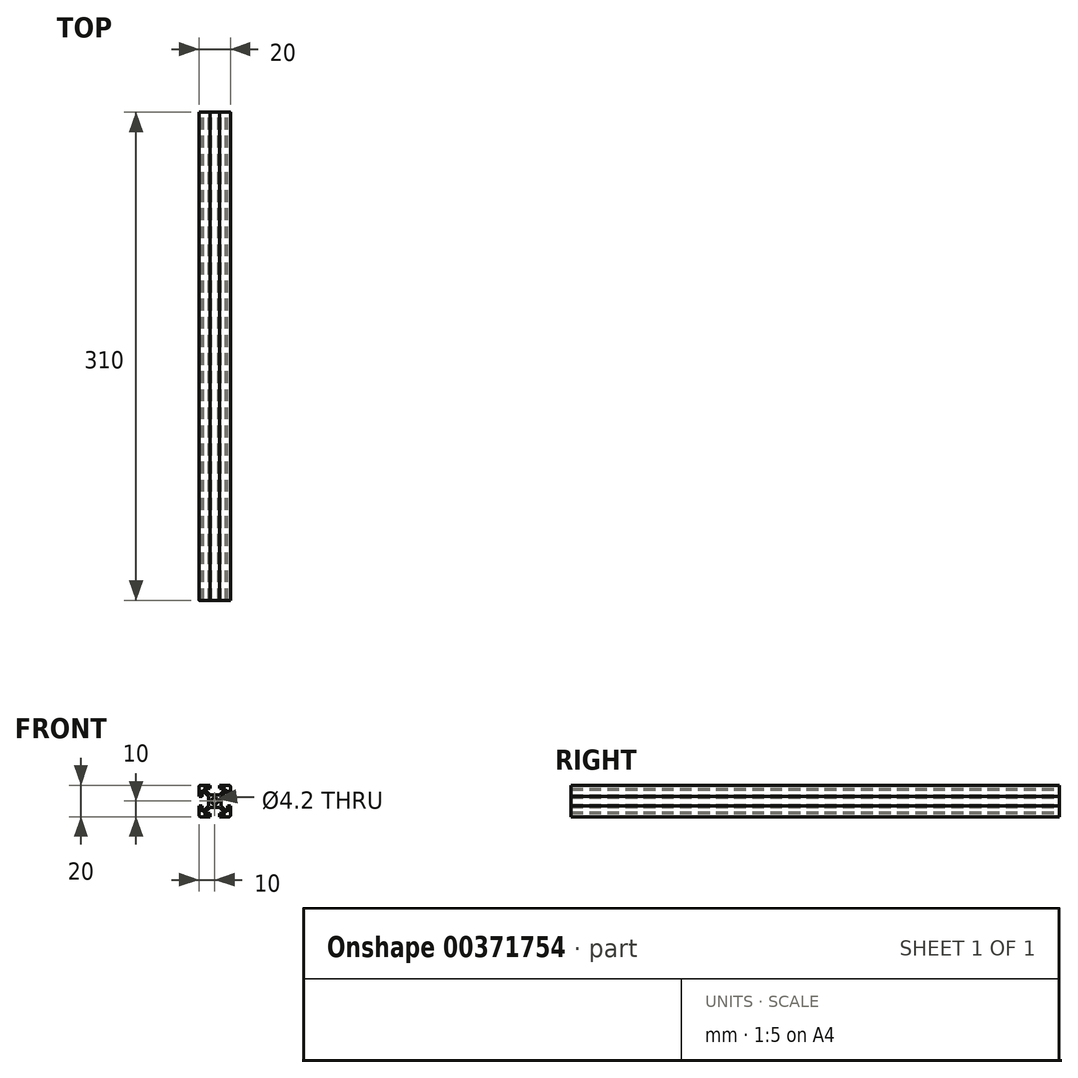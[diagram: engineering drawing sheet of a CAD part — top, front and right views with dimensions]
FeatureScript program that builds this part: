
annotation { "Feature Type Name" : "Feature", "Feature Type Description" : "" }
export const myFeature = defineFeature(function(context is Context, id is Id, definition is map)
    precondition{}
    {
        {
            var Q0;
            Q0=qCreatedBy(makeId("Front.planeOp"),FACE);
            var sketch = newSketch(context, id + "F0", { "sketchPlane" : qUnion([Q0])});
            skLineSegment(sketch, "E0.top", {"start": v(-9, -10) * mm, "end": v(-3, -10) * mm});
            skLineSegment(sketch, "E0.left", {"start": v(-10, 9) * mm, "end": v(-10, 3.08) * mm});
            skLineSegment(sketch, "E0.right", {"start": v(10, 9) * mm, "end": v(10, 3.08) * mm});
            skPoint(sketch, "E0.middle", {"position": v(0, 0) * mm});
            skArc(sketch, "E1.filletArc", {"start": v(-9, 10) * mm, "mid": v(-9.7, 9.7) * mm, "end": v(-10, 9) * mm});
            skArc(sketch, "E2.filletArc", {"start": v(10, 9) * mm, "mid": v(9.7, 9.7) * mm, "end": v(9, 10) * mm});
            skPoint(sketch, "E3.visualSharp", {"position": v(10, -10) * mm});
            skArc(sketch, "E3.filletArc", {"start": v(9, -10) * mm, "mid": v(9.7, -9.7) * mm, "end": v(10, -9) * mm});
            skArc(sketch, "E4.filletArc", {"start": v(-10, -9) * mm, "mid": v(-9.7, -9.7) * mm, "end": v(-9, -10) * mm});
            skCircle(sketch, "E5", {"center": v(0, 0) * mm, "radius": 2.1 * mm});
            skLineSegment(sketch, "E6.bottom", {"start": v(-3, 4) * mm, "end": v(3, 4) * mm});
            skLineSegment(sketch, "E6.top", {"start": v(-3, -4) * mm, "end": v(3, -4) * mm});
            skLineSegment(sketch, "E6.left", {"start": v(-4, 3) * mm, "end": v(-4, -3) * mm});
            skLineSegment(sketch, "E6.right", {"start": v(4, 3) * mm, "end": v(4, -3) * mm});
            skLineSegment(sketch, "E7", {"start": v(-4, 3) * mm, "end": v(-8, 7) * mm});
            skLineSegment(sketch, "E8", {"start": v(-7, 8) * mm, "end": v(-3, 4) * mm});
            skLineSegment(sketch, "E9", {"start": v(3, 4) * mm, "end": v(7, 8) * mm});
            skLineSegment(sketch, "E10", {"start": v(4, 3) * mm, "end": v(8, 7) * mm});
            skLineSegment(sketch, "E11", {"start": v(4, -3) * mm, "end": v(8, -7) * mm});
            skLineSegment(sketch, "E12", {"start": v(3, -4) * mm, "end": v(7, -8) * mm});
            skLineSegment(sketch, "E13", {"start": v(-3, -4) * mm, "end": v(-7, -8) * mm});
            skLineSegment(sketch, "E14", {"start": v(-8, -7) * mm, "end": v(-4, -3) * mm});
            skLineSegment(sketch, "E15.bottom", {"start": v(-7, 8) * mm, "end": v(-3, 8) * mm});
            skLineSegment(sketch, "E15.top", {"start": v(-7, -8) * mm, "end": v(-3, -8) * mm});
            skLineSegment(sketch, "E15.left", {"start": v(-8, 7) * mm, "end": v(-8, 3.18) * mm});
            skLineSegment(sketch, "E15.right", {"start": v(8, 7) * mm, "end": v(8, 3.08) * mm});
            skLineSegment(sketch, "E16", {"start": v(-3, -8) * mm, "end": v(-3, -10) * mm});
            skLineSegment(sketch, "E17", {"start": v(3, -8) * mm, "end": v(3, -10) * mm});
            skLineSegment(sketch, "E18", {"start": v(8, 3.08) * mm, "end": v(10, 3.08) * mm});
            skLineSegment(sketch, "E19", {"start": v(8, -3) * mm, "end": v(10, -3) * mm});
            skLineSegment(sketch, "E20", {"start": v(-3, 10) * mm, "end": v(-3, 8) * mm});
            skLineSegment(sketch, "E21", {"start": v(3, 10) * mm, "end": v(3, 8) * mm});
            skLineSegment(sketch, "E22", {"start": v(-10, 3.08) * mm, "end": v(-8.1, 3.08) * mm});
            skLineSegment(sketch, "E23", {"start": v(-10, -3) * mm, "end": v(-8, -3) * mm});
            skLineSegment(sketch, "E24.trimOffspring", {"start": v(-8, -3) * mm, "end": v(-8, -7) * mm});
            skLineSegment(sketch, "E25.trimOffspring", {"start": v(-10, -3) * mm, "end": v(-10, -9) * mm});
            skLineSegment(sketch, "E26.trimOffspring", {"start": v(3, 10) * mm, "end": v(9, 10) * mm});
            skLineSegment(sketch, "E27.trimOffspring", {"start": v(3, 8) * mm, "end": v(7, 8) * mm});
            skLineSegment(sketch, "E28", {"start": v(-9, 10) * mm, "end": v(-3, 10) * mm});
            skLineSegment(sketch, "E29.trimOffspring", {"start": v(10, -3) * mm, "end": v(10, -9) * mm});
            skLineSegment(sketch, "E30.trimOffspring", {"start": v(8, -3) * mm, "end": v(8, -7) * mm});
            skLineSegment(sketch, "E31.trimOffspring", {"start": v(3, -10) * mm, "end": v(9, -10) * mm});
            skLineSegment(sketch, "E32.trimOffspring", {"start": v(3, -8) * mm, "end": v(7, -8) * mm});
            skPoint(sketch, "E33.visualSharp", {"position": v(-8, 3.08) * mm});
            skArc(sketch, "E33.filletArc", {"start": v(-8.1, 3.08) * mm, "mid": v(-8.03, 3.1) * mm, "end": v(-8, 3.18) * mm});
            skSolve(sketch);
        }
        {
            assignVariable(context, id + "F1", {"name" : "x", "anyValue" : 310});
        }
        {
            var Q0;
            Q0=makeQuery(id+"F0.imprint","IMPRINT",FACE,{"disambiguationData":[TD([[makeQuery(id+"F0.imprint","IMPRINT",EDGE,{"derivedFrom":sQuery(id+"F0.wireOp",EDGE,"E0.top")}),1.0]])]});
            extrude(context, id + "F2", {"entities" : qUnion([Q0]), "depth" : (getVariable(context, 'x')) * mm});
        }
    });
